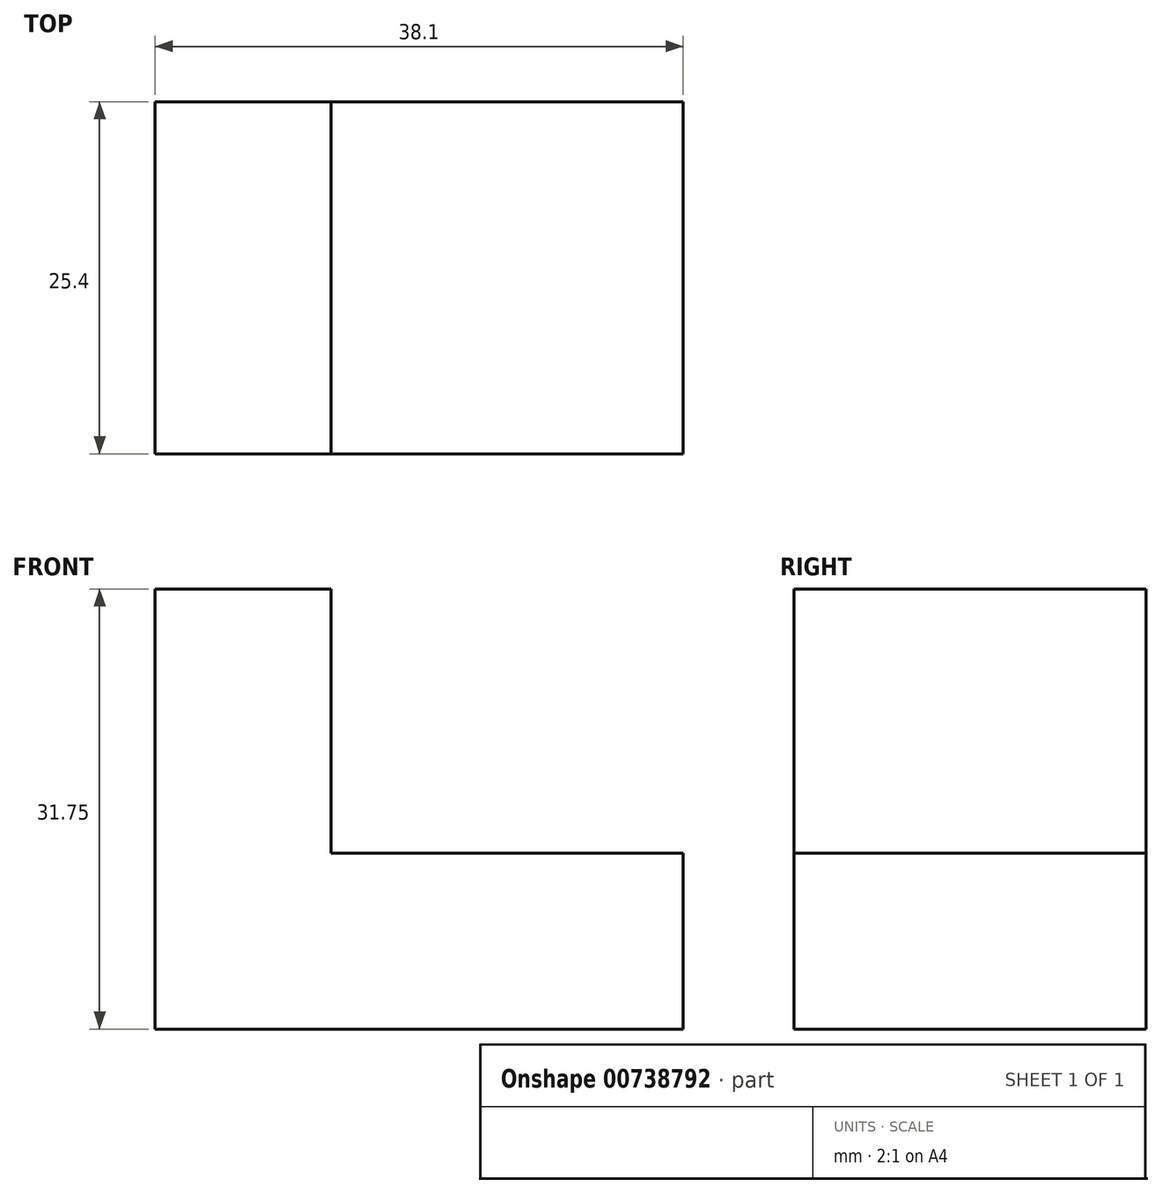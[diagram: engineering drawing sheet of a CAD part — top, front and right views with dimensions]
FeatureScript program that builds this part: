
annotation { "Feature Type Name" : "Feature", "Feature Type Description" : "" }
export const myFeature = defineFeature(function(context is Context, id is Id, definition is map)
    precondition{}
    {
        {
            var Q0;
            Q0=qCreatedBy(makeId("Front.planeOp"),FACE);
            var sketch = newSketch(context, id + "F0", { "sketchPlane" : qUnion([Q0])});
            skLineSegment(sketch, "E0", {"start": v(-17.75, 22.65) * mm, "end": v(-17.75, -9.1) * mm});
            skLineSegment(sketch, "E1", {"start": v(-17.75, -9.1) * mm, "end": v(20.35, -9.1) * mm});
            skLineSegment(sketch, "E2", {"start": v(20.35, -9.1) * mm, "end": v(20.35, 3.6) * mm});
            skLineSegment(sketch, "E3", {"start": v(20.35, 3.6) * mm, "end": v(-5.05, 3.6) * mm});
            skLineSegment(sketch, "E4", {"start": v(-5.05, 3.6) * mm, "end": v(-5.05, 22.65) * mm});
            skLineSegment(sketch, "E5", {"start": v(-5.05, 22.65) * mm, "end": v(-17.75, 22.65) * mm});
            skSolve(sketch);
        }
        {
            var Q0;
            Q0 = qSketchRegion(id + "F0", true);
            extrude(context, id + "F1", {"entities" : qUnion([Q0]), "depth" : 25.4 * mm, "offsetDistance" : 25.4 * mm});
        }
    });
